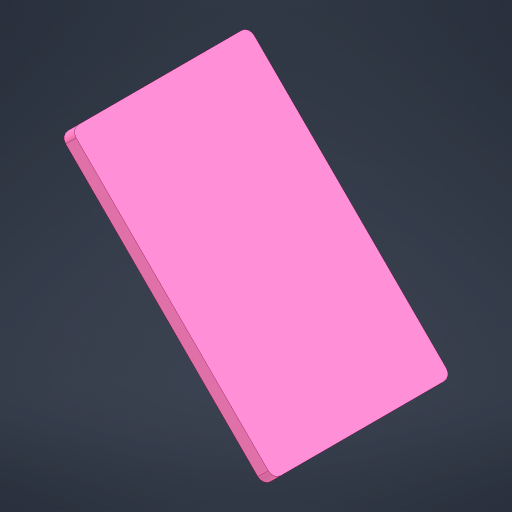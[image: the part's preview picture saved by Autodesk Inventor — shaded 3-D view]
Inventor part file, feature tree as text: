
AUTODESK INVENTOR PART (.ipt)
format: ipt  version: 2023.4 (Build 274418000, 418)  size: 284,672 bytes
history: native  units: mm
features: extrude x9, projected_geometry x4, plane x3, reference x2, other x2, sketch x1, mirror x1, fillet x1
ambient origin geometry x8: Origin, YZ Plane, XZ Plane, XY Plane, X Axis, Y Axis, Z Axis, Center Point
bodies: Solid1 (feature_tree)
feature tree (23):
  plane  "Work Plane1"
  extrude  "Extrusion1"  Depth=2.5mm TaperAngle=0.0deg
  sketch  "Sketch2"  dims[d0=0.075mm d1=2.5mm d2=0.0mm d3=10.0mm d4=10.0mm d5=5.0mm d6=5.0mm d7=2.5mm d8=2.5mm d9=5.0mm d10=31.75mm d11=0.0mm d12=38.75mm d13=22.5mm d14=3.875mm d15=3.875mm d16=3.875mm d17=2.5mm d18=0.0mm d19=2.5mm d20=0.0mm d21=0.75mm d22=5.075mm d23=5.075mm d24=5.075mm d25=1.5mm d26=0.0mm d27=32.5mm d28=1.5mm d29=0.0mm d30=2.5mm d31=0.0mm d32=2.5mm d33=0.0mm d34=10.0mm d35=0.0mm d36=1.25mm]
  extrude  "Extrusion2"  Depth=10.0mm
  extrude  "Extrusion3"  Depth=10.0mm
  extrude  "Extrusion4"  Depth=1.25mm
  extrude  "Extrusion5"  Depth=1.25mm
  extrude  "Extrusion6"  Depth=2.5mm
  plane  "Work Plane2"
  extrude  "Extrusion7"  Depth=2.5mm
  plane  "Work Plane3"
  mirror  "Mirror1"
  extrude  "Extrusion8"  Depth=1.25mm
  extrude  "Extrusion9"  Depth=1.25mm TaperAngle=0.0deg
  fillet  "Fillet1"  Radius=38.75mm
  reference  "Reference1"
  projected_geometry  "Projected Loop1"
  projected_geometry  "Projected Loop2"
  projected_geometry  "Projected Loop3"
  reference  "Reference2"
  projected_geometry  "Projected Loop4"
  other  "Cube 1x1 V5.iam"
  other  "Cube 1x1 Bottom V5:1"
